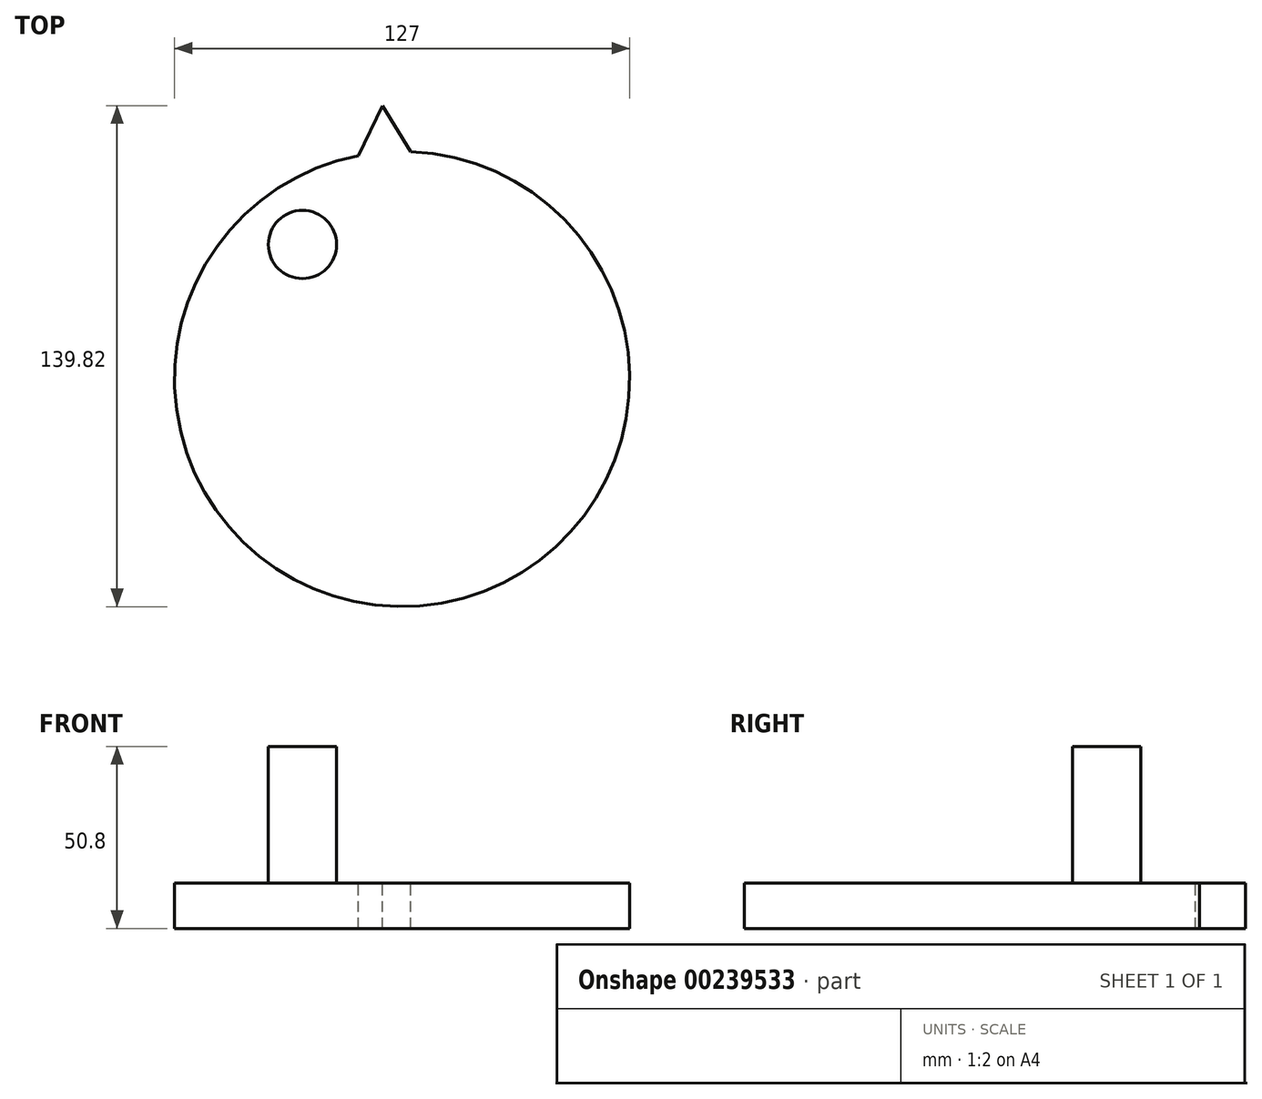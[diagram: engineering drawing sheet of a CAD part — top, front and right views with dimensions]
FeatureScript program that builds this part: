
annotation { "Feature Type Name" : "Feature", "Feature Type Description" : "" }
export const myFeature = defineFeature(function(context is Context, id is Id, definition is map)
    precondition{}
    {
        {
            var Q0;
            Q0=qCreatedBy(makeId("Top.planeOp"),FACE);
            var sketch = newSketch(context, id + "F0", { "sketchPlane" : qUnion([Q0])});
            skCircle(sketch, "E0", {"center": v(0, 0) * mm, "radius": 63.5 * mm});
            skSolve(sketch);
        }
        {
            var Q0;
            Q0 = qSketchRegion(id + "F0", true);
            extrude(context, id + "F1", {"entities" : qUnion([Q0]), "depth" : 12.7 * mm});
        }
        {
            var Q0;
            Q0=makeQuery(id+"F1.opExtrude","CAP_FACE",FACE,{"disambiguationData":[OSD([sQuery(id+"F0.wireOp",EDGE,"E0")])],"isStart":false});
            var sketch = newSketch(context, id + "F2", { "sketchPlane" : qUnion([Q0])});
            skCircle(sketch, "E1", {"center": v(-27.78, 37.55) * mm, "radius": 9.53 * mm});
            skSolve(sketch);
        }
        {
            var Q0;
            Q0 = qSketchRegion(id + "F2", true);
            extrude(context, id + "F3", {"entities" : qUnion([Q0]), "operationType" : NewBodyOperationType.ADD, "depth" : 38.1 * mm});
        }
        {
            var Q0;
            Q0=makeQuery(id+"F1.opExtrude","CAP_FACE",FACE,{"disambiguationData":[OSD([sQuery(id+"F0.wireOp",EDGE,"E0")])],"isStart":false});
            var sketch = newSketch(context, id + "F4", { "sketchPlane" : qUnion([Q0])});
            skLineSegment(sketch, "E2", {"start": v(-12.15, 62.33) * mm, "end": v(-5.5, 76.32) * mm});
            skLineSegment(sketch, "E3", {"start": v(-5.5, 76.32) * mm, "end": v(2.4, 63.45) * mm});
            skSolve(sketch);
        }
        {
            var Q0;
            {var subQ0=sQuery(id+"F4.wireOp",EDGE,"E2");Q0=makeQuery(id+"F4.imprint","IMPRINT",FACE,{"disambiguationData":[TD([[makeQuery(id+"F4.imprint","IMPRINT",EDGE,{"derivedFrom":subQ0}),-1.0]])]});}
            extrude(context, id + "F5", {"entities" : qUnion([Q0]), "operationType" : NewBodyOperationType.ADD, "oppositeDirection" : true, "depth" : 12.7 * mm});
        }
    });
